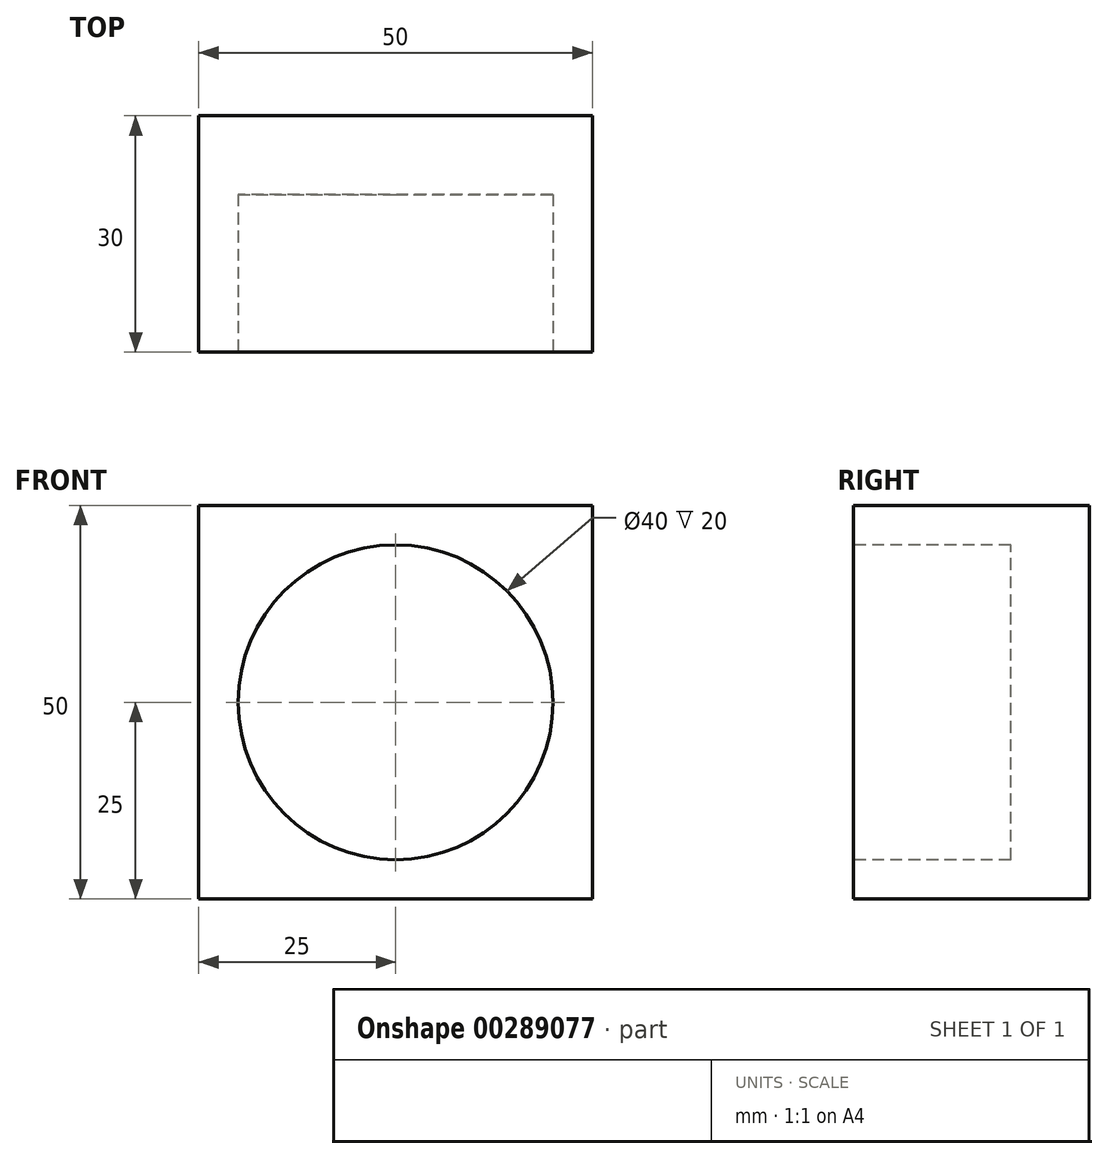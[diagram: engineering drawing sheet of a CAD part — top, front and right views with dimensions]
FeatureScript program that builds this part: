
annotation { "Feature Type Name" : "Feature", "Feature Type Description" : "" }
export const myFeature = defineFeature(function(context is Context, id is Id, definition is map)
    precondition{}
    {
        {
            var Q0;
            Q0=qCreatedBy(makeId("Front.planeOp"),FACE);
            var sketch = newSketch(context, id + "F0", { "sketchPlane" : qUnion([Q0])});
            skLineSegment(sketch, "E0.bottom", {"start": v(25, -25) * mm, "end": v(-25, -25) * mm});
            skLineSegment(sketch, "E0.top", {"start": v(25, 25) * mm, "end": v(-25, 25) * mm});
            skLineSegment(sketch, "E0.left", {"start": v(25, -25) * mm, "end": v(25, 25) * mm});
            skLineSegment(sketch, "E0.right", {"start": v(-25, -25) * mm, "end": v(-25, 25) * mm});
            skPoint(sketch, "E0.middle", {"position": v(0, 0) * mm});
            skSolve(sketch);
        }
        {
            var Q0;
            Q0=makeQuery(id+"F0.imprint","IMPRINT",FACE,{"disambiguationData":[TD([[makeQuery(id+"F0.imprint","IMPRINT",EDGE,{"derivedFrom":sQuery(id+"F0.wireOp",EDGE,"E0.bottom")}),-1.0]])]});
            extrude(context, id + "F1", {"entities" : qUnion([Q0]), "depth" : 30 * mm});
        }
        {
            var Q0;
            Q0=makeQuery(id+"F1.opExtrude","CAP_FACE",FACE,{"disambiguationData":[OSD([sQuery(id+"F0.wireOp",EDGE,"E0.bottom"),sQuery(id+"F0.wireOp",EDGE,"E0.top"),sQuery(id+"F0.wireOp",EDGE,"E0.left"),sQuery(id+"F0.wireOp",EDGE,"E0.right")])],"isStart":false});
            var sketch = newSketch(context, id + "F2", { "sketchPlane" : qUnion([Q0])});
            skCircle(sketch, "E1", {"center": v(0, 0) * mm, "radius": 20 * mm});
            skSolve(sketch);
        }
        {
            var Q0;
            Q0=makeQuery(id+"F2.imprint","IMPRINT",FACE,{"disambiguationData":[TD([[makeQuery(id+"F2.imprint","IMPRINT",EDGE,{"derivedFrom":sQuery(id+"F2.wireOp",EDGE,"E1")}),1.0]])]});
            extrude(context, id + "F3", {"entities" : qUnion([Q0]), "operationType" : NewBodyOperationType.REMOVE, "oppositeDirection" : true, "depth" : 20 * mm});
        }
    });
